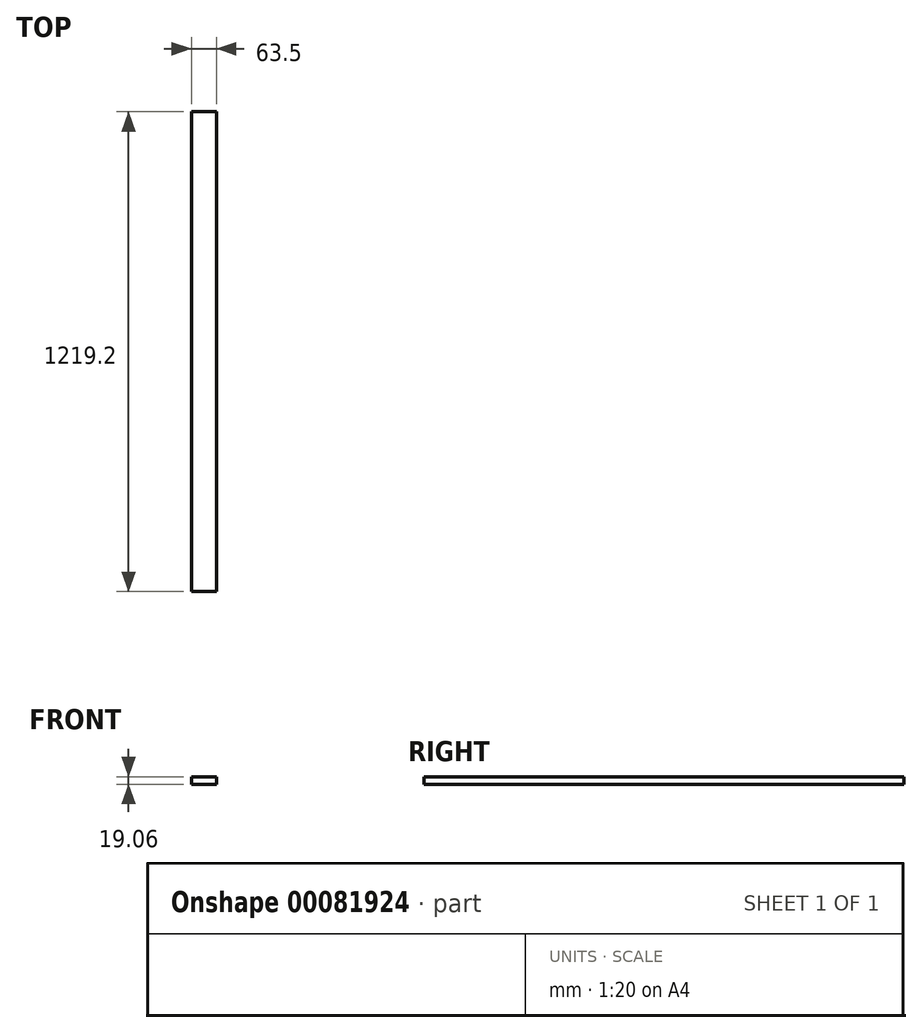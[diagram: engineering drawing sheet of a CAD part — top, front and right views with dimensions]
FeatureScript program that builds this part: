
annotation { "Feature Type Name" : "Feature", "Feature Type Description" : "" }
export const myFeature = defineFeature(function(context is Context, id is Id, definition is map)
    precondition{}
    {
        {
            var Q0;
            Q0=qCreatedBy(makeId("Front.planeOp"),FACE);
            var sketch = newSketch(context, id + "F0", { "sketchPlane" : qUnion([Q0])});
            skLineSegment(sketch, "E0.bottom", {"start": v(-31.75, 9.53) * mm, "end": v(31.75, 9.53) * mm});
            skLineSegment(sketch, "E0.top", {"start": v(-31.75, -9.52) * mm, "end": v(31.75, -9.52) * mm});
            skLineSegment(sketch, "E0.left", {"start": v(-31.75, 9.53) * mm, "end": v(-31.75, -9.52) * mm});
            skLineSegment(sketch, "E0.right", {"start": v(31.75, 9.53) * mm, "end": v(31.75, -9.52) * mm});
            skPoint(sketch, "E0.middle", {"position": v(0, 0) * mm});
            skSolve(sketch);
        }
        {
            var Q0;
            Q0=qSketchRegion(id+"F0",true);
            extrude(context, id + "F1", {"entities" : qUnion([Q0]), "endBound" : BoundingType.SYMMETRIC, "depth" : 1219.2 * mm});
        }
    });
